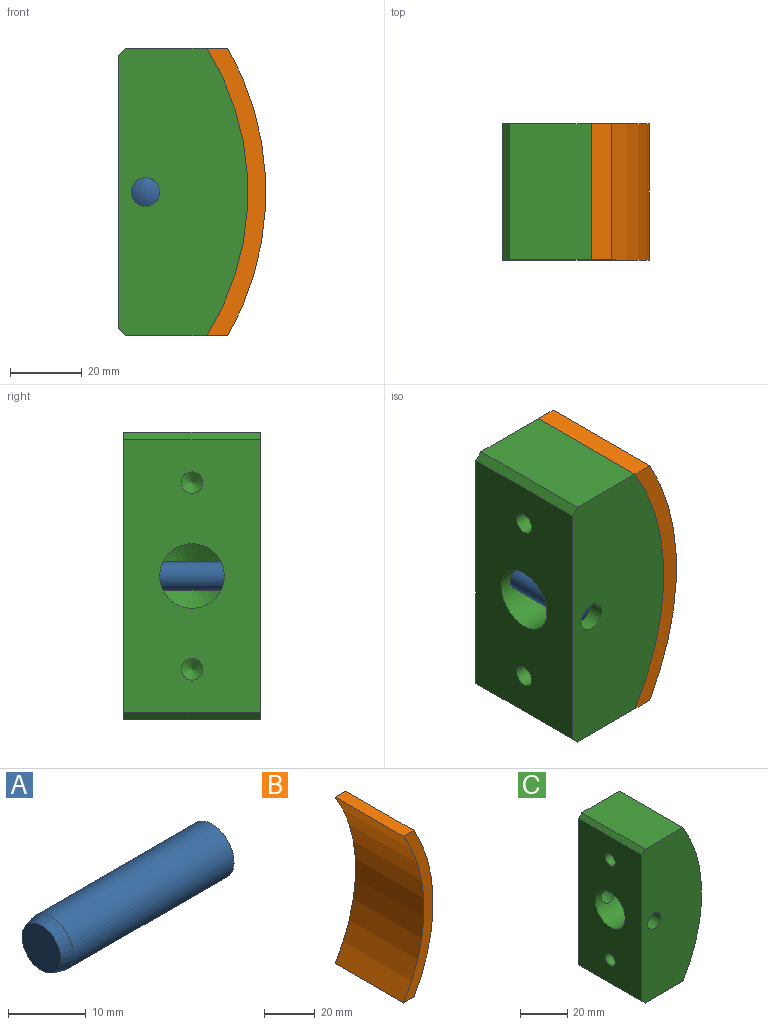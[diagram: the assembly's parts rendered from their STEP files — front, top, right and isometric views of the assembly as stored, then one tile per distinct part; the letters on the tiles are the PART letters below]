
ASSEMBLY  parts=3 mates=2
PART A: 4 faces, bbox 32x8x8 mm
  f0: cone r=3.76mm half-angle=15deg, axis (1,0,0), area 44mm2, adj f1,f3
  f1: cylinder r=4mm len=29.13mm, axis (-1,0,0), area 732.1mm2, adj f0,f2
  f2: sphere r=8mm, area 53.9mm2, adj f1
  f3: plane 7.04x7.04mm, normal (-1,0,0), area 38.9mm2, adj f0
PART B: 6 faces, bbox 16.4x38x80 mm
  f0: plane 80x16.38mm, normal (0,1,0), area 419.7mm2, adj f1,f3,f4,f5
  f1: plane 38x5.81mm, normal (0,0,-1), area 220.9mm2, adj f0,f2,f3,f4
  f2: plane 80x16.38mm, normal (0,-1,0), area 419.7mm2, adj f1,f3,f4,f5
  f3: cylinder r=76mm len=80mm, axis (0,-1,0), area 3201.4mm2, adj f0,f1,f2,f5
  f4: cylinder r=81mm len=80mm, axis (0,-1,0), area 3179.5mm2, adj f0,f1,f2,f5
  f5: plane 38x5.81mm, normal (0,0,1), area 220.9mm2, adj f0,f2,f3,f4
PART C: 16 faces, bbox 36x38x80 mm
  f0: cylinder r=4mm len=10.94mm, axis (0,-1,0), area 262.9mm2, adj f2,f12
  f1: cylinder r=4mm len=10.94mm, axis (0,-1,0), area 263mm2, adj f7,f12
  f2: plane 80x36mm, normal (0,1,0), area 2532mm2, adj f0,f3,f4,f5,f6,f14,f15
  f3: plane 38x22.62mm, normal (0,0,-1), area 859.6mm2, adj f2,f4,f7,f14
  f4: cylinder r=76mm len=80mm, axis (0,-1,0), area 3201.4mm2, adj f2,f3,f5,f7
  f5: plane 38x22.62mm, normal (0,0,1), area 859.6mm2, adj f2,f4,f7,f15
  f6: plane 76x38mm, normal (-1,0,0), area 2577mm2, adj f2,f7,f9,f11,f12,f14,f15
  f7: plane 80x36mm, normal (0,-1,0), area 2532mm2, adj f1,f3,f4,f5,f6,f14,f15
  f8: cone r=0mm half-angle=59deg, axis (-1,0,0), area 33mm2, adj f9
  f9: cylinder r=3mm len=15mm, axis (-1,0,0), area 282.7mm2, adj f6,f8
  f10: cone r=0mm half-angle=59deg, axis (-1,0,0), area 33mm2, adj f11
  f11: cylinder r=3mm len=15mm, axis (-1,0,0), area 282.7mm2, adj f6,f10
  f12: cylinder r=9mm len=18mm, axis (-1,0,0), area 745.1mm2, adj f0,f1,f6,f13
  f13: cone r=0mm half-angle=59deg, axis (-1,0,0), area 296.9mm2, adj f12
  f14: plane 38x2mm, normal (-0.71,0,-0.71), area 107.5mm2, adj f2,f3,f6,f7
  f15: plane 38x2mm, normal (-0.71,0,0.71), area 107.5mm2, adj f2,f5,f6,f7
PLACE A rot(axis=(0.58,-0.58,-0.58),120deg) t=(47.5,-6.14,0)mm
PLACE B at identity
PLACE C at identity fixed
MATE fastened B.f3 <-> C.f4  axis (0,-1,0) through (0,-41.5,0)mm
MATE fastened A.f0 <-> C.f0  axis (0,1,0) through (47.5,-22.5,0)mm
